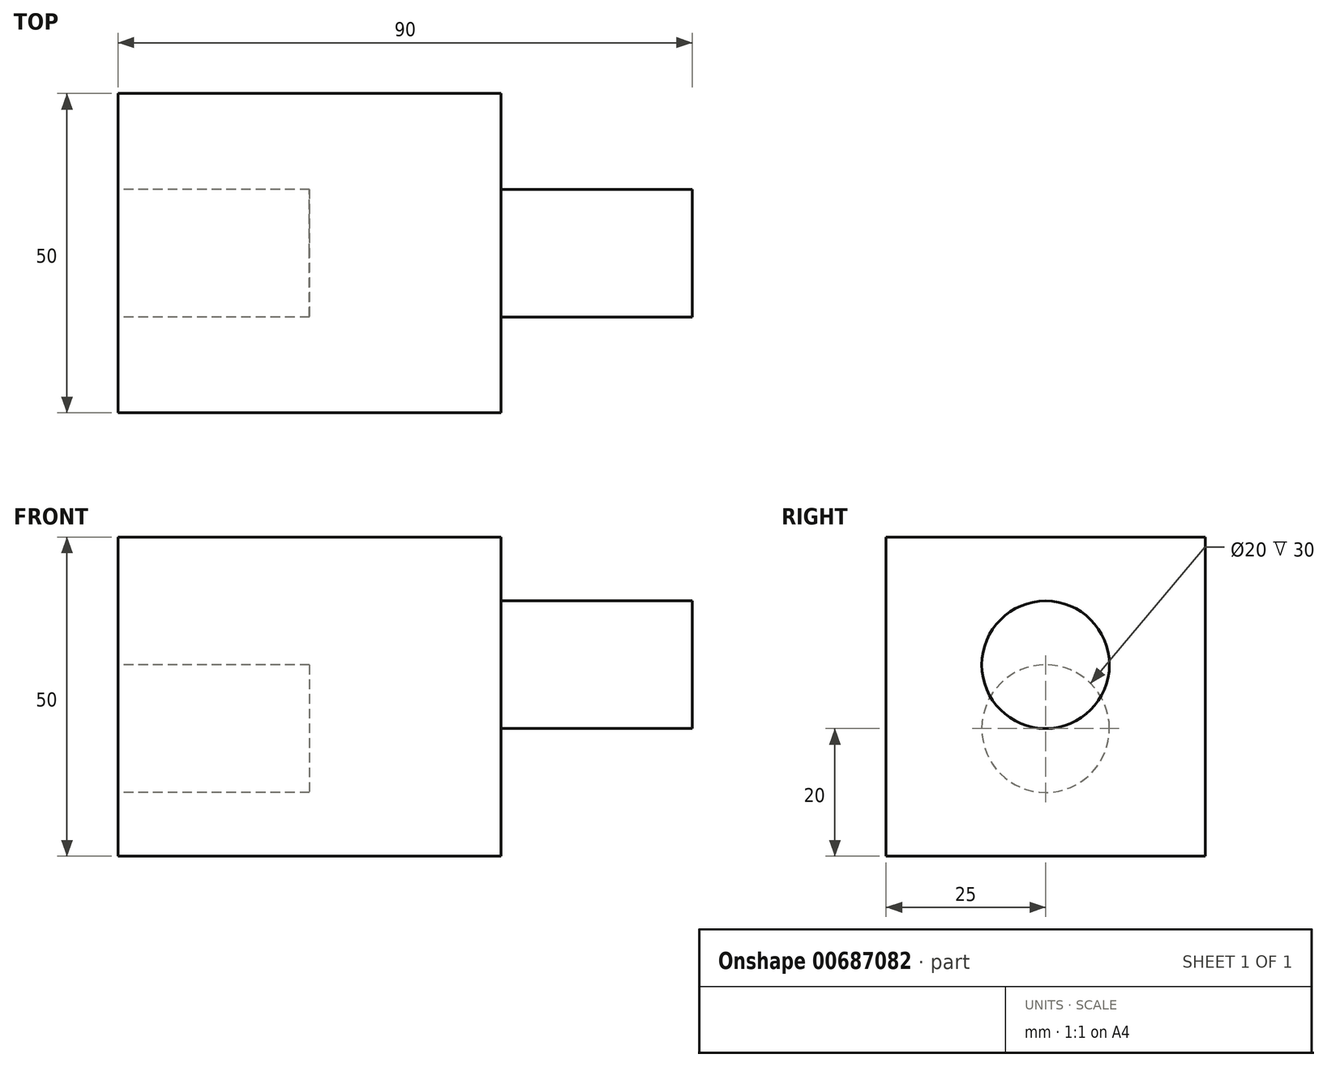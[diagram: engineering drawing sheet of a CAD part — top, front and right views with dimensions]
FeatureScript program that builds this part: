
annotation { "Feature Type Name" : "Feature", "Feature Type Description" : "" }
export const myFeature = defineFeature(function(context is Context, id is Id, definition is map)
    precondition{}
    {
        {
            var Q0;
            Q0=qCreatedBy(makeId("Top.planeOp"),FACE);
            var sketch = newSketch(context, id + "F0", { "sketchPlane" : qUnion([Q0])});
            skLineSegment(sketch, "E0.bottom", {"start": v(30, 25) * mm, "end": v(-30, 25) * mm});
            skLineSegment(sketch, "E0.top", {"start": v(30, -25) * mm, "end": v(-30, -25) * mm});
            skLineSegment(sketch, "E0.left", {"start": v(30, 25) * mm, "end": v(30, -25) * mm});
            skLineSegment(sketch, "E0.right", {"start": v(-30, 25) * mm, "end": v(-30, -25) * mm});
            skPoint(sketch, "E0.middle", {"position": v(0, 0) * mm});
            skSolve(sketch);
        }
        {
            var Q0;
            Q0 = qSketchRegion(id + "F0", true);
            extrude(context, id + "F1", {"entities" : qUnion([Q0]), "depth" : 50 * mm, "offsetDistance" : 25 * mm});
        }
        {
            var Q0;
            Q0=makeQuery(id+"F1.opExtrude","SWEPT_FACE",FACE,{"disambiguationData":[OSD([sQuery(id+"F0.wireOp",EDGE,"E0.left")])]});
            var sketch = newSketch(context, id + "F2", { "sketchPlane" : qUnion([Q0])});
            skCircle(sketch, "E1", {"center": v(0, 30) * mm, "radius": 10 * mm});
            skSolve(sketch);
        }
        {
            var Q0;
            Q0 = qSketchRegion(id + "F2", true);
            extrude(context, id + "F3", {"entities" : qUnion([Q0]), "operationType" : NewBodyOperationType.ADD, "depth" : 30 * mm, "offsetDistance" : 25 * mm});
        }
        {
            var Q0;
            Q0=makeQuery(id+"F1.opExtrude","SWEPT_FACE",FACE,{"disambiguationData":[OSD([sQuery(id+"F0.wireOp",EDGE,"E0.right")])]});
            var sketch = newSketch(context, id + "F4", { "sketchPlane" : qUnion([Q0])});
            skCircle(sketch, "E2", {"center": v(0, 20) * mm, "radius": 10 * mm});
            skSolve(sketch);
        }
        {
            var Q0;
            Q0 = qSketchRegion(id + "F4", true);
            extrude(context, id + "F5", {"entities" : qUnion([Q0]), "operationType" : NewBodyOperationType.REMOVE, "oppositeDirection" : true, "depth" : 30 * mm, "offsetDistance" : 25 * mm});
        }
    });
